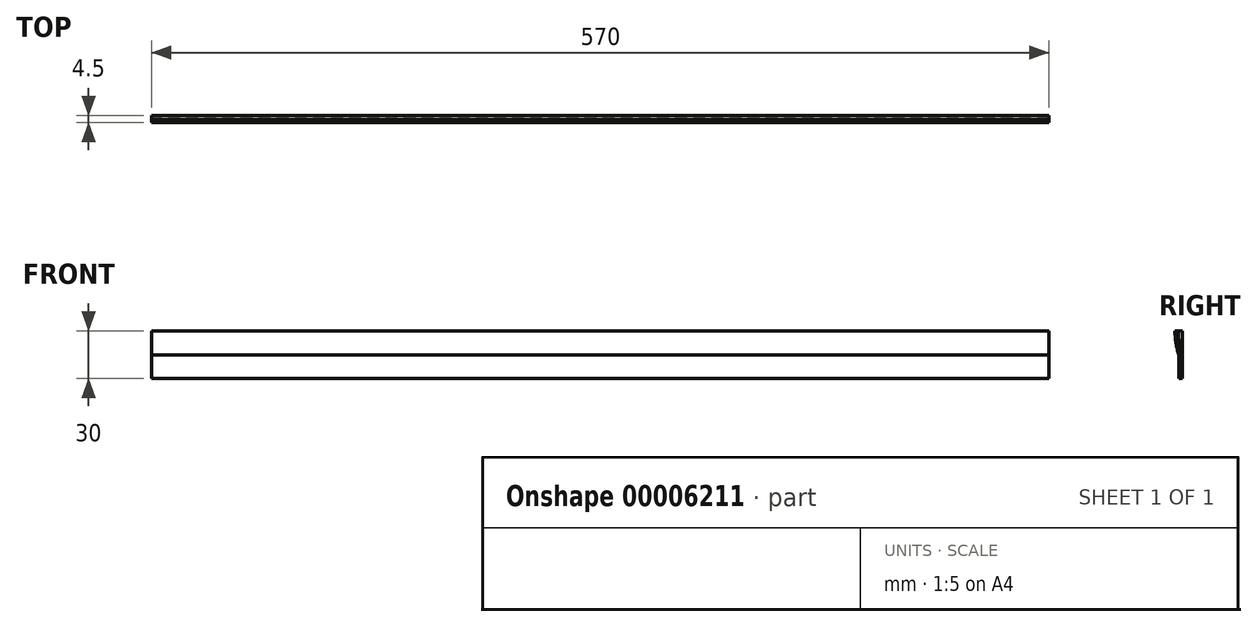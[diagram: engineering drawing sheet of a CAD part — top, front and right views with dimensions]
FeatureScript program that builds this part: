
annotation { "Feature Type Name" : "Feature", "Feature Type Description" : "" }
export const myFeature = defineFeature(function(context is Context, id is Id, definition is map)
    precondition{}
    {
        {
            var Q0;
            Q0=qCreatedBy(makeId("Right.planeOp"),FACE);
            var sketch = newSketch(context, id + "F0", { "sketchPlane" : qUnion([Q0])});
            skLineSegment(sketch, "E0.rect.bottom", {"start": v(2.5, -15) * mm, "end": v(0, -15) * mm});
            skLineSegment(sketch, "E0.rect.top", {"start": v(-0.5, 15) * mm, "end": v(-2.5, 15) * mm});
            skPoint(sketch, "E0.rect.middle", {"position": v(0, 0) * mm});
            skLineSegment(sketch, "E1", {"start": v(0, 0) * mm, "end": v(0, -15) * mm});
            skArc(sketch, "E2", {"start": v(-2.5, 15) * mm, "mid": v(-1.87, 7.4) * mm, "end": v(0, 0) * mm});
            skPoint(sketch, "E3.orphan", {"position": v(-2.5, -15) * mm});
            skLineSegment(sketch, "E4.0", {"start": v(2, 0.34) * mm, "end": v(2, -15) * mm});
            skArc(sketch, "E4.1", {"start": v(-0.5, 15) * mm, "mid": v(0.13, 7.56) * mm, "end": v(2, 0.34) * mm});
            skPoint(sketch, "E0.rect.left.end.orphan", {"position": v(2.5, 15) * mm});
            skSolve(sketch);
        }
        {
            var Q0;
            Q0=makeQuery(id+"F0.imprint","IMPRINT",FACE,{"disambiguationData":[TD([[makeQuery(id+"F0.imprint","IMPRINT",EDGE,{"derivedFrom":sQuery(id+"F0.wireOp",EDGE,"E0.rect.top")}),1.0]])]});
            extrude(context, id + "F1", {"entities" : qUnion([Q0]), "depth" : 570 * mm});
        }
        {
            var Q0;
            Q0=makeQuery(id+"F1.opExtrude","CAP_FACE",FACE,{"disambiguationData":[OSD([sQuery(id+"F0.wireOp",EDGE,"E0.rect.bottom"),sQuery(id+"F0.wireOp",EDGE,"E0.rect.top"),sQuery(id+"F0.wireOp",EDGE,"E1"),sQuery(id+"F0.wireOp",EDGE,"E2"),sQuery(id+"F0.wireOp",EDGE,"E4.0"),sQuery(id+"F0.wireOp",EDGE,"E4.1")])],"isStart":false});
            var sketch = newSketch(context, id + "F2", { "sketchPlane" : qUnion([Q0])});
            skLineSegment(sketch, "E5", {"start": v(-0.5, 15) * mm, "end": v(2, 15) * mm});
            skLineSegment(sketch, "E6", {"start": v(2, 15) * mm, "end": v(2, 0.34) * mm});
            skArc(sketch, "E7.0", {"start": v(-0.5, 15) * mm, "mid": v(0.13, 7.56) * mm, "end": v(2, 0.34) * mm});
            skSolve(sketch);
        }
        {
            var Q0;
            Q0=makeQuery(id+"F2.imprint","IMPRINT",FACE,{"disambiguationData":[TD([[makeQuery(id+"F2.imprint","IMPRINT",EDGE,{"derivedFrom":sQuery(id+"F2.wireOp",EDGE,"E5")}),-1.0]])]});
            extrude(context, id + "F3", {"entities" : qUnion([Q0]), "oppositeDirection" : true, "depth" : 570 * mm});
        }
    });
